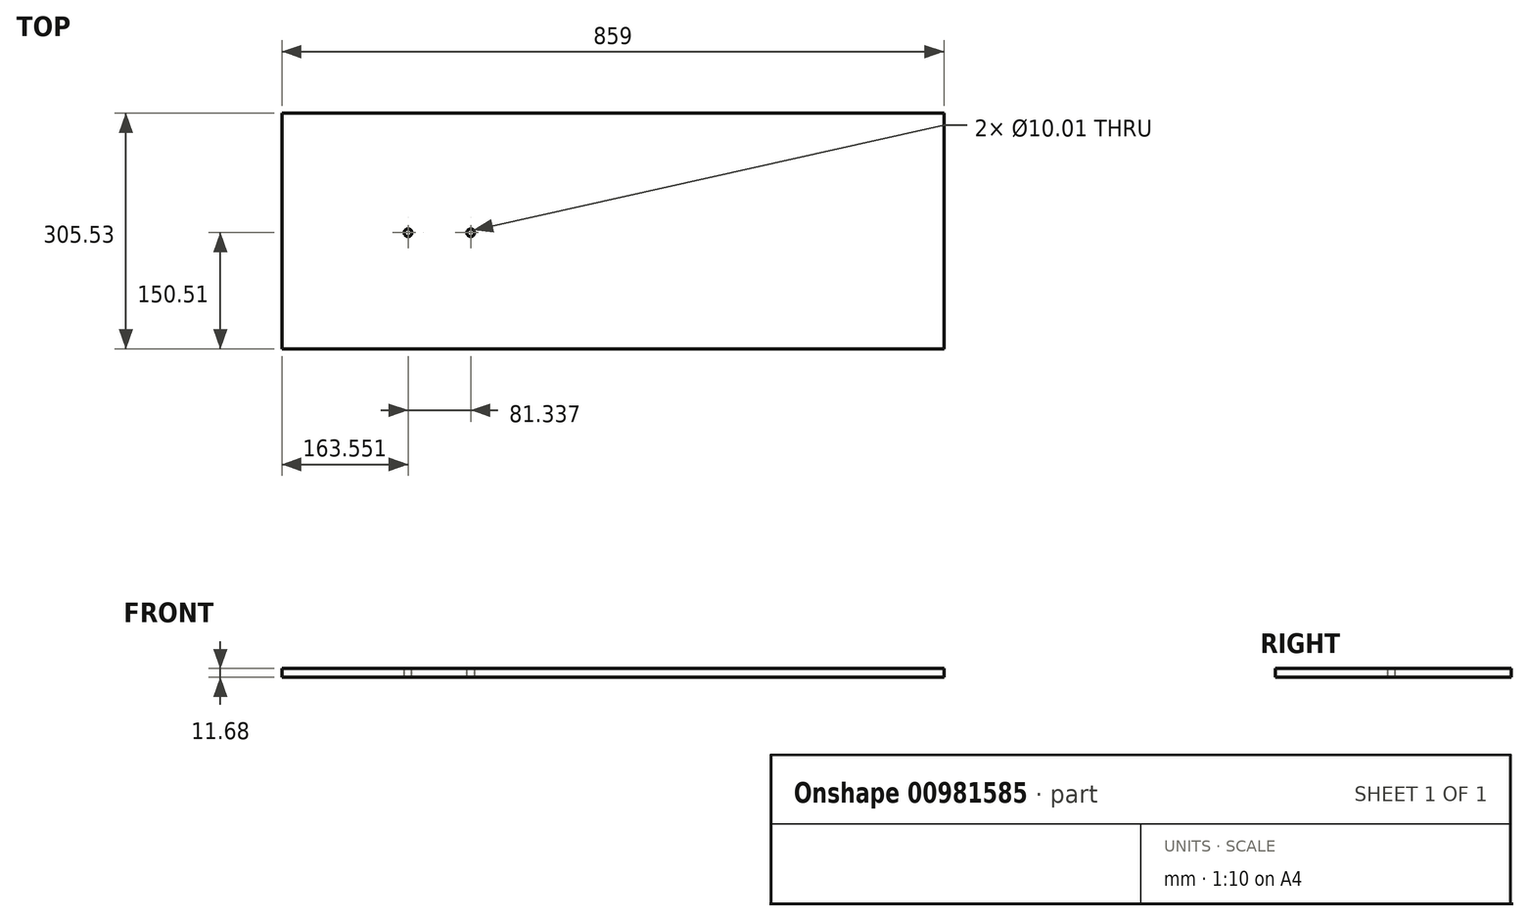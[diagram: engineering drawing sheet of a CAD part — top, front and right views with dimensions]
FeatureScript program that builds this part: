
annotation { "Feature Type Name" : "Feature", "Feature Type Description" : "" }
export const myFeature = defineFeature(function(context is Context, id is Id, definition is map)
    precondition{}
    {
        {
            var Q0;
            Q0=qCreatedBy(makeId("Top.planeOp"),FACE);
            var sketch = newSketch(context, id + "F0", { "sketchPlane" : qUnion([Q0])});
            skLineSegment(sketch, "E0.bottom", {"start": v(-204.22, 155.02) * mm, "end": v(654.78, 155.02) * mm});
            skLineSegment(sketch, "E0.top", {"start": v(-204.22, -150.5) * mm, "end": v(654.78, -150.5) * mm});
            skLineSegment(sketch, "E0.left", {"start": v(-204.22, 155.02) * mm, "end": v(-204.22, -150.5) * mm});
            skLineSegment(sketch, "E0.right", {"start": v(654.78, 155.02) * mm, "end": v(654.78, -150.5) * mm});
            skSolve(sketch);
        }
        {
            var Q0;
            Q0 = qSketchRegion(id + "F0", true);
            extrude(context, id + "F1", {"entities" : qUnion([Q0]), "depth" : 11.68 * mm, "offsetDistance" : 25.4 * mm});
        }
        {
            var Q0;
            Q0=makeQuery(id+"F1.opExtrude","CAP_FACE",FACE,{"disambiguationData":[OSD([sQuery(id+"F0.wireOp",EDGE,"E0.bottom"),sQuery(id+"F0.wireOp",EDGE,"E0.top"),sQuery(id+"F0.wireOp",EDGE,"E0.left"),sQuery(id+"F0.wireOp",EDGE,"E0.right")])],"isStart":false});
            var sketch = newSketch(context, id + "F2", { "sketchPlane" : qUnion([Q0])});
            skCircle(sketch, "E1", {"center": v(-40.67, 0) * mm, "radius": 5 * mm});
            skCircle(sketch, "E2.MirrorC", {"center": v(40.67, 0) * mm, "radius": 5 * mm});
            skSolve(sketch);
        }
        {
            var Q0;
            Q0 = qSketchRegion(id + "F2", true);
            extrude(context, id + "F3", {"entities" : qUnion([Q0]), "operationType" : NewBodyOperationType.REMOVE, "oppositeDirection" : true, "depth" : 25.4 * mm, "offsetDistance" : 25.4 * mm});
        }
    });
